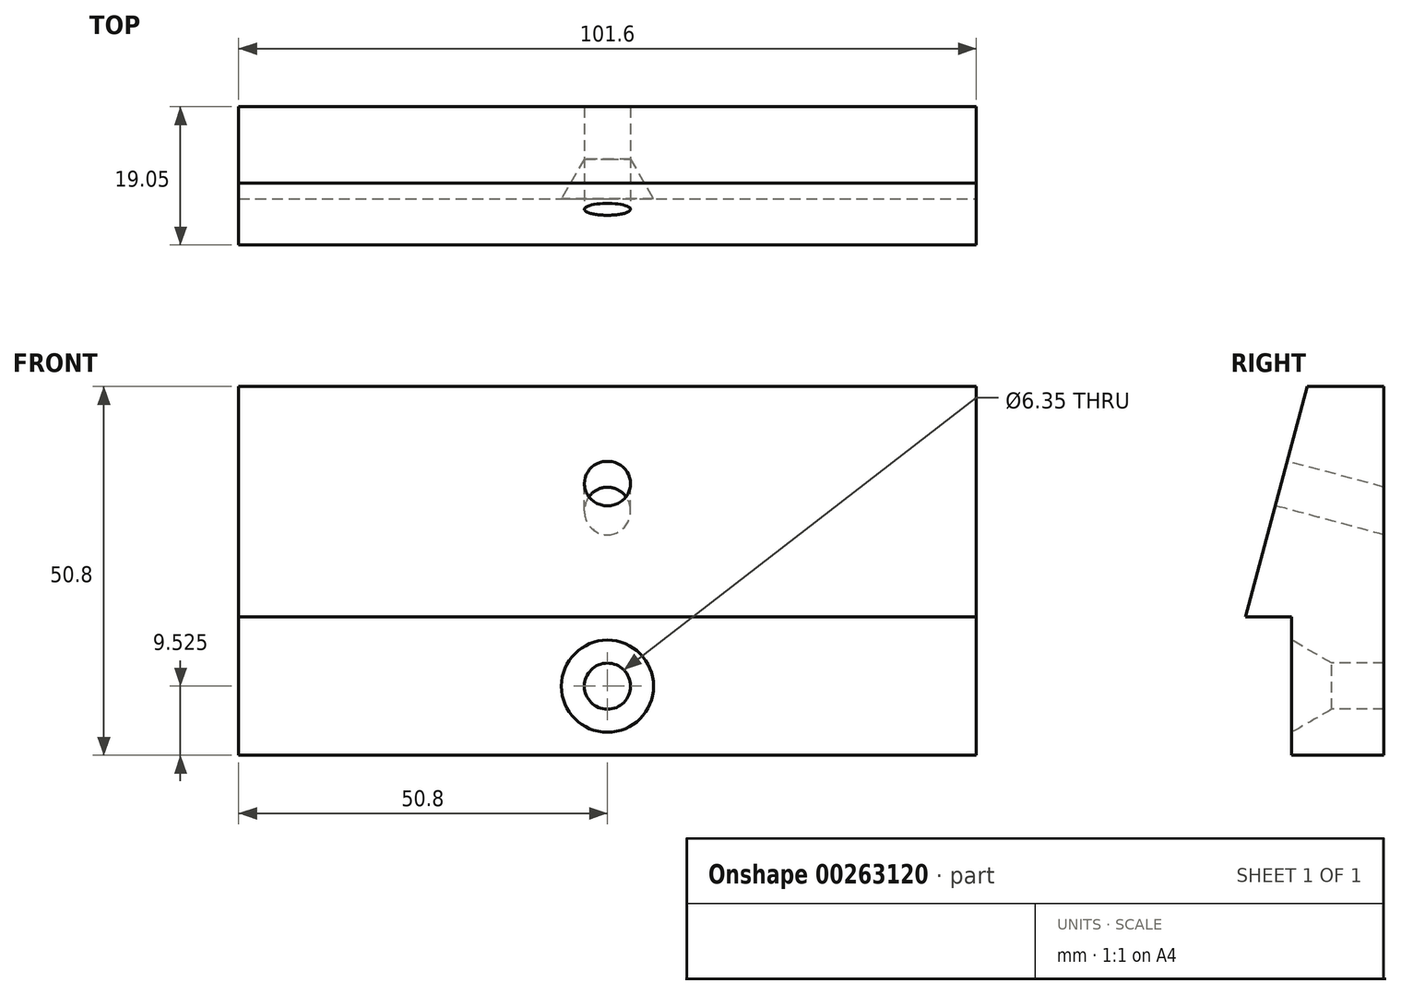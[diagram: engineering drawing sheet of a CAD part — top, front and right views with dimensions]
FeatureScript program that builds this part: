
annotation { "Feature Type Name" : "Feature", "Feature Type Description" : "" }
export const myFeature = defineFeature(function(context is Context, id is Id, definition is map)
    precondition{}
    {
        {
            var Q0;
            Q0=qCreatedBy(makeId("Front.planeOp"),FACE);
            var sketch = newSketch(context, id + "F0", { "sketchPlane" : qUnion([Q0])});
            skLineSegment(sketch, "E0.bottom", {"start": v(-50.8, 50.8) * mm, "end": v(50.8, 50.8) * mm});
            skLineSegment(sketch, "E0.top", {"start": v(-50.8, 0) * mm, "end": v(50.8, 0) * mm});
            skLineSegment(sketch, "E0.left", {"start": v(-50.8, 50.8) * mm, "end": v(-50.8, 0) * mm});
            skLineSegment(sketch, "E0.right", {"start": v(50.8, 50.8) * mm, "end": v(50.8, 0) * mm});
            skLineSegment(sketch, "E1.bottom", {"start": v(0, 0) * mm, "end": v(0, 0) * mm});
            skLineSegment(sketch, "E1.top", {"start": v(0, 50.8) * mm, "end": v(0, 50.8) * mm});
            skLineSegment(sketch, "E1.left", {"start": v(0, 0) * mm, "end": v(0, 50.8) * mm});
            skLineSegment(sketch, "E1.right", {"start": v(0, 0) * mm, "end": v(0, 50.8) * mm});
            skSolve(sketch);
        }
        {
            var Q0;
            Q0=qSketchRegion(id+"F0",true);
            extrude(context, id + "F1", {"entities" : qUnion([Q0]), "oppositeDirection" : true, "depth" : 19.05 * mm});
        }
        {
            var Q0;
            Q0=makeQuery(id+"F1.opExtrude","SWEPT_FACE",FACE,{"disambiguationData":[OSD([sQuery(id+"F0.wireOp",EDGE,"E0.right")])]});
            var sketch = newSketch(context, id + "F2", { "sketchPlane" : qUnion([Q0])});
            skLineSegment(sketch, "E2", {"start": v(0, 19.05) * mm, "end": v(8.5, 50.8) * mm});
            skLineSegment(sketch, "E3", {"start": v(8.5, 50.8) * mm, "end": v(0, 50.8) * mm});
            skLineSegment(sketch, "E4", {"start": v(0, 50.8) * mm, "end": v(0, 19.05) * mm});
            skLineSegment(sketch, "E5.bottom", {"start": v(0, 0) * mm, "end": v(6.35, 0) * mm});
            skLineSegment(sketch, "E5.top", {"start": v(0, 19.05) * mm, "end": v(6.35, 19.05) * mm});
            skLineSegment(sketch, "E5.left", {"start": v(0, 0) * mm, "end": v(0, 19.05) * mm});
            skLineSegment(sketch, "E5.right", {"start": v(6.35, 0) * mm, "end": v(6.35, 19.05) * mm});
            skSolve(sketch);
        }
        {
            var Q0;
            Q0 = qSketchRegion(id + "F2", true);
            extrude(context, id + "F3", {"entities" : qUnion([Q0]), "operationType" : NewBodyOperationType.REMOVE, "endBound" : BoundingType.THROUGH_ALL, "oppositeDirection" : true, "depth" : 25.4 * mm});
        }
        {
            var Q0;
            Q0=makeQuery(id+"F3.boolean.opBoolean","COPY",FACE,{"derivedFrom":makeQuery(id+"F3.opExtrude","SWEPT_FACE",FACE,{"disambiguationData":[OSD([sQuery(id+"F2.wireOp",EDGE,"E2")])]})});
            var sketch = newSketch(context, id + "F4", { "sketchPlane" : qUnion([Q0])});
            skCircle(sketch, "E6", {"center": v(0, 37.45) * mm, "radius": 3.18 * mm});
            skSolve(sketch);
        }
        {
            var Q0;
            Q0 = qSketchRegion(id + "F4", true);
            extrude(context, id + "F5", {"entities" : qUnion([Q0]), "operationType" : NewBodyOperationType.REMOVE, "endBound" : BoundingType.THROUGH_ALL, "oppositeDirection" : true, "depth" : 25.4 * mm});
        }
        {
            var Q0;
            Q0=makeQuery(id+"F3.boolean.opBoolean","COPY",FACE,{"derivedFrom":makeQuery(id+"F3.opExtrude","SWEPT_FACE",FACE,{"disambiguationData":[OSD([sQuery(id+"F2.wireOp",EDGE,"E5.right")])]})});
            var sketch = newSketch(context, id + "F6", { "sketchPlane" : qUnion([Q0])});
            skCircle(sketch, "E7", {"center": v(0, 9.53) * mm, "radius": 3.18 * mm});
            skSolve(sketch);
        }
        {
            var Q0;
            Q0 = qSketchRegion(id + "F6", true);
            extrude(context, id + "F7", {"entities" : qUnion([Q0]), "operationType" : NewBodyOperationType.REMOVE, "endBound" : BoundingType.THROUGH_ALL, "oppositeDirection" : true, "depth" : 25.4 * mm});
        }
        {
            var Q0;
            Q0=makeQuery(id+"F3.boolean.opBoolean","COPY",FACE,{"derivedFrom":makeQuery(id+"F3.opExtrude","SWEPT_FACE",FACE,{"disambiguationData":[OSD([sQuery(id+"F2.wireOp",EDGE,"E5.right")])]})});
            var sketch = newSketch(context, id + "F8", { "sketchPlane" : qUnion([Q0])});
            skCircle(sketch, "E8", {"center": v(0, 9.53) * mm, "radius": 6.35 * mm});
            skSolve(sketch);
        }
        {
            var Q0;
            Q0 = qSketchRegion(id + "F8", true);
            extrude(context, id + "F9", {"entities" : qUnion([Q0]), "operationType" : NewBodyOperationType.REMOVE, "oppositeDirection" : true, "depth" : 6.35 * mm, "hasDraft" : true, "draftAngle" : 30 * degree, "draftPullDirection" : true});
        }
    });
